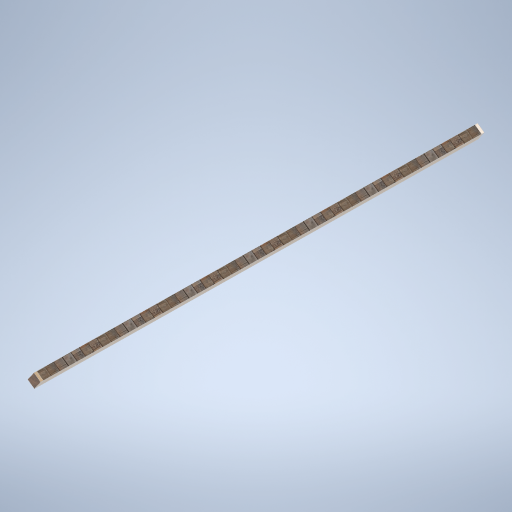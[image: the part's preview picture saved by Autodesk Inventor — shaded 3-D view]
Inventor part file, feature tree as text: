
AUTODESK INVENTOR PART (.ipt)
format: ipt  version: 2024.2 (Build 282272000, 272)  size: 313,344 bytes
history: native  units: mm
features: sketch x5, plane x2, extrude x2, projected_geometry x2, loft x1
ambient origin geometry x8: Origin, YZ Plane, XZ Plane, XY Plane, X Axis, Y Axis, Z Axis, Center Point
bodies: Solid1 (feature_tree)
feature tree (12):
  sketch  "Sketch1"  dims[d0=0.0mm d1=8101.0mm d2=0.0mm d3=90.0deg]
  plane  "Work Plane2"
  loft  "Loft1"
  sketch  "Sketch3"  dims[d8=50.0mm d9=0.0mm]
  sketch  "Sketch4"
  extrude  "Extrusion1"  Depth=50.0mm TaperAngle=0.0deg
  extrude  "Extrusion2"  [1 undecoded]
  plane  "Work Plane1"
  sketch  "Sketch2"  dims[d4=0.0mm d5=90.0deg d6=50.0mm d7=0.0mm]
  projected_geometry  "Projected Loop1"
  projected_geometry  "Projected Loop2"
  sketch  "Sketch5"
note: 1 required parameter value undecoded (feature->parameter linkage not recoverable at this tier; creation-order binding heuristic only, values carry confidence <= 0.55)
